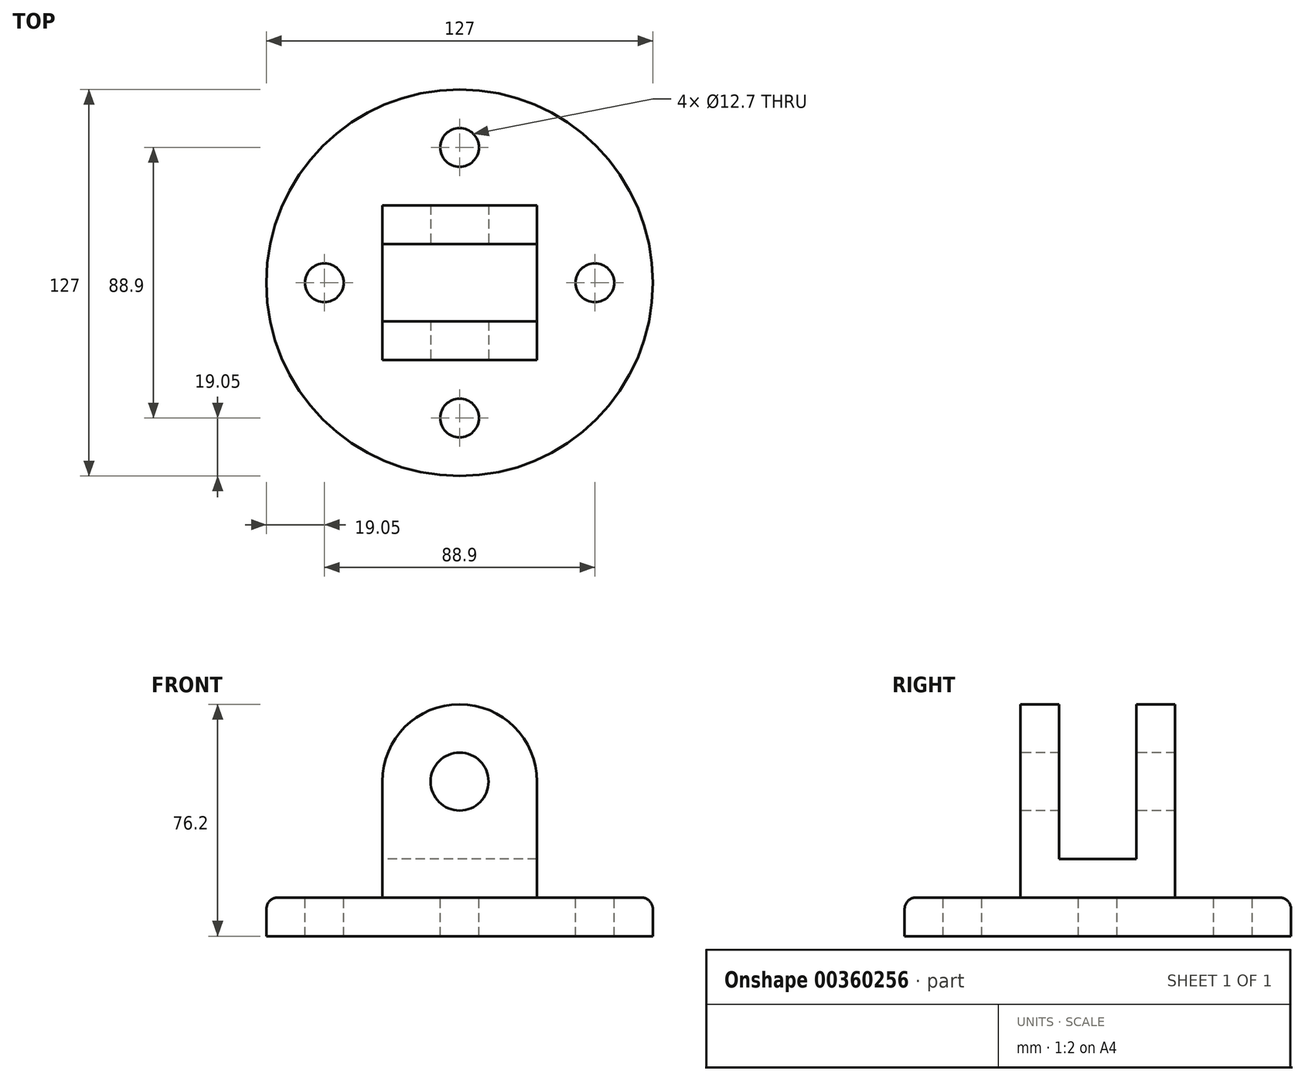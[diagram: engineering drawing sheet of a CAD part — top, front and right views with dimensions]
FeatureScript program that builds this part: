
annotation { "Feature Type Name" : "Feature", "Feature Type Description" : "" }
export const myFeature = defineFeature(function(context is Context, id is Id, definition is map)
    precondition{}
    {
        {
            var Q0;
            Q0=qCreatedBy(makeId("Top.planeOp"),FACE);
            var sketch = newSketch(context, id + "F0", { "sketchPlane" : qUnion([Q0])});
            skCircle(sketch, "E0", {"center": v(0, 0) * mm, "radius": 63.5 * mm});
            skSolve(sketch);
        }
        {
            var Q0;
            Q0 = qSketchRegion(id + "F0", true);
            extrude(context, id + "F1", {"entities" : qUnion([Q0]), "depth" : 12.7 * mm});
        }
        {
            var Q0;
            Q0=makeQuery(id+"F1.opExtrude","CAP_FACE",FACE,{"disambiguationData":[OSD([sQuery(id+"F0.wireOp",EDGE,"E0")])],"isStart":false});
            var sketch = newSketch(context, id + "F2", { "sketchPlane" : qUnion([Q0])});
            skCircle(sketch, "E1", {"center": v(0, 44.45) * mm, "radius": 6.35 * mm});
            skCircle(sketch, "E2", {"center": v(-44.45, 0) * mm, "radius": 6.35 * mm});
            skCircle(sketch, "E3", {"center": v(0, -44.45) * mm, "radius": 6.35 * mm});
            skCircle(sketch, "E4", {"center": v(44.45, 0) * mm, "radius": 6.35 * mm});
            skCircle(sketch, "E5", {"center": v(0, 0) * mm, "radius": 44.45 * mm, "construction": true});
            skSolve(sketch);
        }
        {
            var Q0;
            Q0 = qSketchRegion(id + "F2", true);
            extrude(context, id + "F3", {"entities" : qUnion([Q0]), "operationType" : NewBodyOperationType.REMOVE, "endBound" : BoundingType.THROUGH_ALL, "oppositeDirection" : true, "depth" : 25.4 * mm});
        }
        {
            var Q0;
            Q0=qCreatedBy(makeId("Front.planeOp"),FACE);
            var sketch = newSketch(context, id + "F4", { "sketchPlane" : qUnion([Q0])});
            skLineSegment(sketch, "E6", {"start": v(0, 0) * mm, "end": v(0, 50.8) * mm, "construction": true});
            skLineSegment(sketch, "E7", {"start": v(-25.4, 50.8) * mm, "end": v(25.4, 50.8) * mm});
            skLineSegment(sketch, "E8.0", {"start": v(-25.4, 12.7) * mm, "end": v(25.4, 12.7) * mm});
            skLineSegment(sketch, "E9", {"start": v(-25.4, 50.8) * mm, "end": v(-25.4, 12.7) * mm});
            skLineSegment(sketch, "E10", {"start": v(25.4, 50.8) * mm, "end": v(25.4, 12.7) * mm});
            skArc(sketch, "E11", {"start": v(25.4, 50.8) * mm, "mid": v(0, 76.2) * mm, "end": v(-25.4, 50.8) * mm});
            skSolve(sketch);
        }
        {
            var Q0;
            Q0 = qSketchRegion(id + "F4", true);
            extrude(context, id + "F5", {"entities" : qUnion([Q0]), "operationType" : NewBodyOperationType.ADD, "endBound" : BoundingType.SYMMETRIC, "depth" : 50.8 * mm});
        }
        {
            var Q0;
            Q0=makeQuery(id+"F5.opExtrude","CAP_FACE",FACE,{"disambiguationData":[OSD([sQuery(id+"F4.wireOp",EDGE,"E8.0"),sQuery(id+"F4.wireOp",EDGE,"E9"),sQuery(id+"F4.wireOp",EDGE,"E10"),sQuery(id+"F4.wireOp",EDGE,"E11")])],"isStart":false});
            var sketch = newSketch(context, id + "F6", { "sketchPlane" : qUnion([Q0])});
            skCircle(sketch, "E12", {"center": v(0, 50.8) * mm, "radius": 9.53 * mm});
            skSolve(sketch);
        }
        {
            var Q0;
            Q0 = qSketchRegion(id + "F6", true);
            extrude(context, id + "F7", {"entities" : qUnion([Q0]), "operationType" : NewBodyOperationType.REMOVE, "endBound" : BoundingType.THROUGH_ALL, "oppositeDirection" : true, "depth" : 25.4 * mm});
        }
        {
            var Q0;
            Q0=makeQuery(id+"F5.opExtrude","SWEPT_FACE",FACE,{"disambiguationData":[OSD([sQuery(id+"F4.wireOp",EDGE,"E9")])]});
            var sketch = newSketch(context, id + "F8", { "sketchPlane" : qUnion([Q0])});
            skLineSegment(sketch, "E13", {"start": v(-12.7, 76.2) * mm, "end": v(12.7, 76.2) * mm});
            skLineSegment(sketch, "E14.top", {"start": v(-12.7, 25.4) * mm, "end": v(12.7, 25.4) * mm});
            skLineSegment(sketch, "E14.left", {"start": v(-12.7, 76.2) * mm, "end": v(-12.7, 25.4) * mm});
            skLineSegment(sketch, "E14.right", {"start": v(12.7, 76.2) * mm, "end": v(12.7, 25.4) * mm});
            skSolve(sketch);
        }
        {
            var Q0;
            Q0 = qSketchRegion(id + "F8", true);
            extrude(context, id + "F9", {"entities" : qUnion([Q0]), "operationType" : NewBodyOperationType.REMOVE, "endBound" : BoundingType.THROUGH_ALL, "oppositeDirection" : true, "depth" : 25.4 * mm});
        }
        {
            var Q0;
            Q0=makeQuery(id+"F5.opExtrude","CAP_EDGE",EDGE,{"disambiguationData":[OSD([sQuery(id+"F4.wireOp",EDGE,"E8.0")])],"isStart":false});
            var Q1;
            Q1=makeQuery(id+"F5.opExtrude","SWEPT_EDGE",EDGE,{"disambiguationData":[OSD([sQuery(id+"F4.wireOp",EDGE,"E8.0"),sQuery(id+"F4.wireOp",EDGE,"E10")])]});
            var Q2;
            Q2=makeQuery(id+"F1.opExtrude","CAP_EDGE",EDGE,{"disambiguationData":[OSD([sQuery(id+"F0.wireOp",EDGE,"E0")])],"isStart":false});
            var Q3;
            Q3=makeQuery(id+"F5.opExtrude","CAP_EDGE",EDGE,{"disambiguationData":[OSD([sQuery(id+"F4.wireOp",EDGE,"E8.0")])],"isStart":true});
            var Q4;
            Q4=makeQuery(id+"F5.opExtrude","SWEPT_EDGE",EDGE,{"disambiguationData":[OSD([sQuery(id+"F4.wireOp",EDGE,"E8.0"),sQuery(id+"F4.wireOp",EDGE,"E9")])]});
            fillet(context, id + "F10", {"entities" : qUnion([Q0, Q1, Q2, Q3, Q4]), "radius" : 3.8 * mm, "tangentPropagation" : true, "allowEdgeOverflow" : false});
        }
    });
